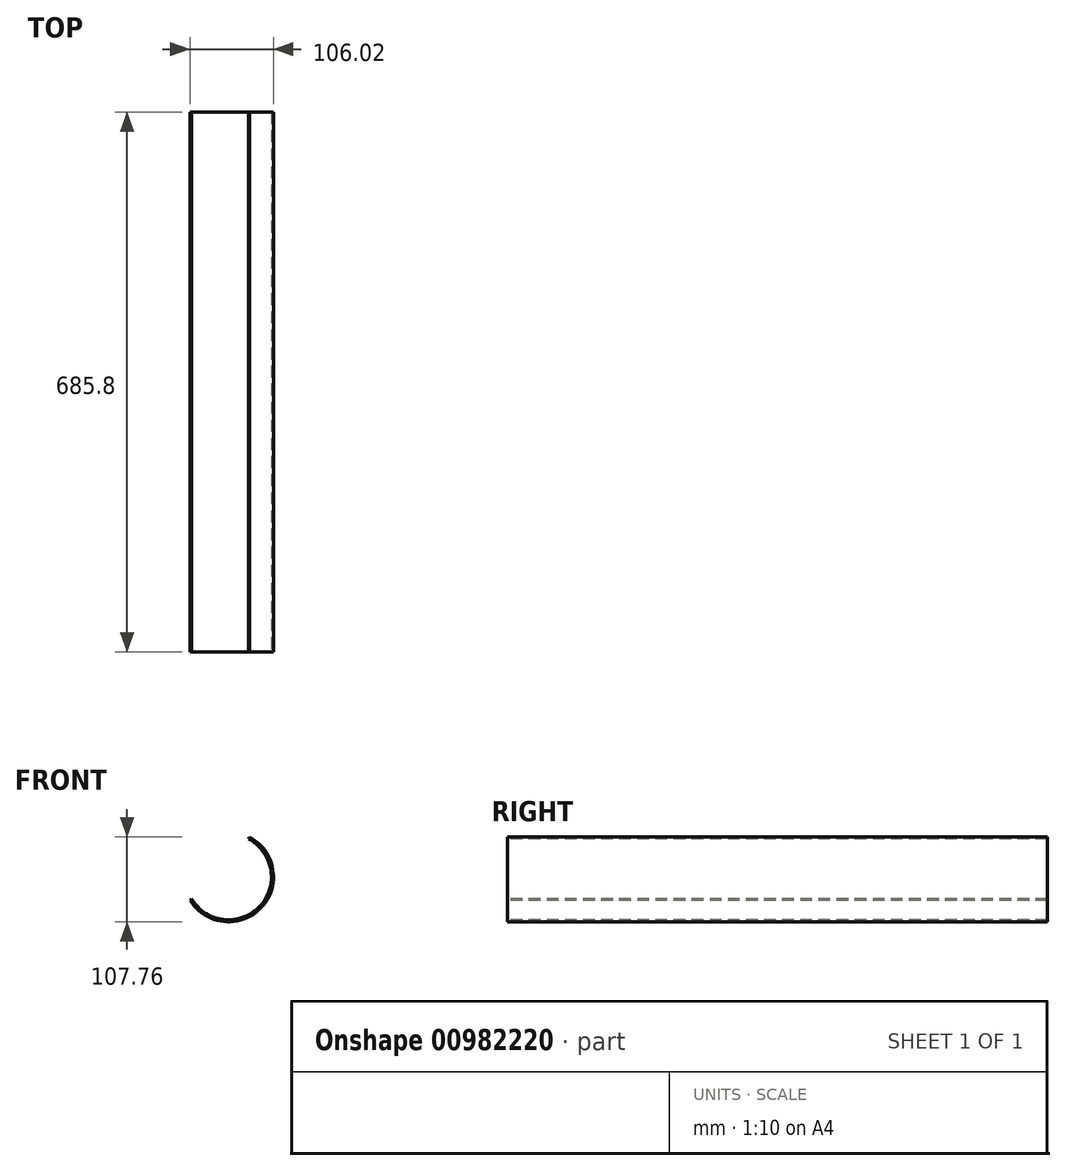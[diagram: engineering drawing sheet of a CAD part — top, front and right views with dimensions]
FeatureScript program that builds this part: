
annotation { "Feature Type Name" : "Feature", "Feature Type Description" : "" }
export const myFeature = defineFeature(function(context is Context, id is Id, definition is map)
    precondition{}
    {
        {
            var Q0;
            Q0=qCreatedBy(makeId("Front.planeOp"),FACE);
            var sketch = newSketch(context, id + "F0", { "sketchPlane" : qUnion([Q0])});
            skLineSegment(sketch, "E0", {"start": v(0, 69.98) * mm, "end": v(0, -68.47) * mm, "construction": true});
            skLineSegment(sketch, "E1", {"start": v(-68.47, 0) * mm, "end": v(66.96, 0) * mm, "construction": true});
            skLineSegment(sketch, "E2", {"start": v(66.96, 0) * mm, "end": v(0, -68.47) * mm, "construction": true});
            skLineSegment(sketch, "E3", {"start": v(-68.47, 0) * mm, "end": v(0, -68.47) * mm, "construction": true});
            skLineSegment(sketch, "E4", {"start": v(-68.47, 0) * mm, "end": v(0, 69.98) * mm, "construction": true});
            skLineSegment(sketch, "E5", {"start": v(0, 69.98) * mm, "end": v(66.96, 0) * mm, "construction": true});
            skCircle(sketch, "E6", {"center": v(0, 0) * mm, "radius": 54.61 * mm});
            skCircle(sketch, "E7.0", {"center": v(0, 0) * mm, "radius": 57.15 * mm});
            skSolve(sketch);
        }
        {
            var Q0;
            Q0=makeQuery(id+"F0.imprint","IMPRINT",FACE,{"disambiguationData":[TD([[makeQuery(id+"F0.imprint","IMPRINT",EDGE,{"derivedFrom":sQuery(id+"F0.wireOp",EDGE,"E6")}),-1.0]])]});
            extrude(context, id + "F1", {"entities" : qUnion([Q0]), "oppositeDirection" : true, "depth" : 685.8 * mm, "offsetDistance" : 25.4 * mm});
        }
        {
            var Q0;
            Q0=makeQuery(id+"F1.opExtrude","CAP_FACE",FACE,{"disambiguationData":[OSD([sQuery(id+"F0.wireOp",EDGE,"E6"),sQuery(id+"F0.wireOp",EDGE,"E7.0")])],"isStart":true});
            var sketch = newSketch(context, id + "F2", { "sketchPlane" : qUnion([Q0])});
            skLineSegment(sketch, "E8", {"start": v(0, 0) * mm, "end": v(26.55, 50.6) * mm});
            skLineSegment(sketch, "E9", {"start": v(-48.87, -29.62) * mm, "end": v(0, 0) * mm});
            skArc(sketch, "E10", {"start": v(26.55, 50.6) * mm, "mid": v(-41.72, 39.22) * mm, "end": v(-48.87, -29.62) * mm});
            skArc(sketch, "E11.0", {"start": v(25, 47.69) * mm, "mid": v(-39.31, 36.96) * mm, "end": v(-46.05, -27.9) * mm});
            skSolve(sketch);
        }
        {
            var Q0;
            {var subQ1=sQuery(id+"F2.wireOp",EDGE,"E8");var subQ4=makeQuery(id+"F1.opExtrude","CAP_EDGE",EDGE,{"disambiguationData":[OSD([sQuery(id+"F0.wireOp",EDGE,"E6")])],"isStart":true});var subQ5=makeQuery(id+"F2.imprint","INTERSECT",VERTEX,{"derivedFrom":[subQ4,subQ1]});Q0=makeQuery(id+"F2.imprint","IMPRINT",FACE,{"disambiguationData":[TD([[makeQuery(id+"F2.imprint","IMPRINT",EDGE,{"disambiguationData":[TD([[subQ5,-1.0]])],"derivedFrom":subQ4}),-1.0]])]});}
            extrude(context, id + "F3", {"entities" : qUnion([Q0]), "operationType" : NewBodyOperationType.REMOVE, "oppositeDirection" : true, "depth" : 685.8 * mm, "offsetDistance" : 25.4 * mm});
        }
    });
